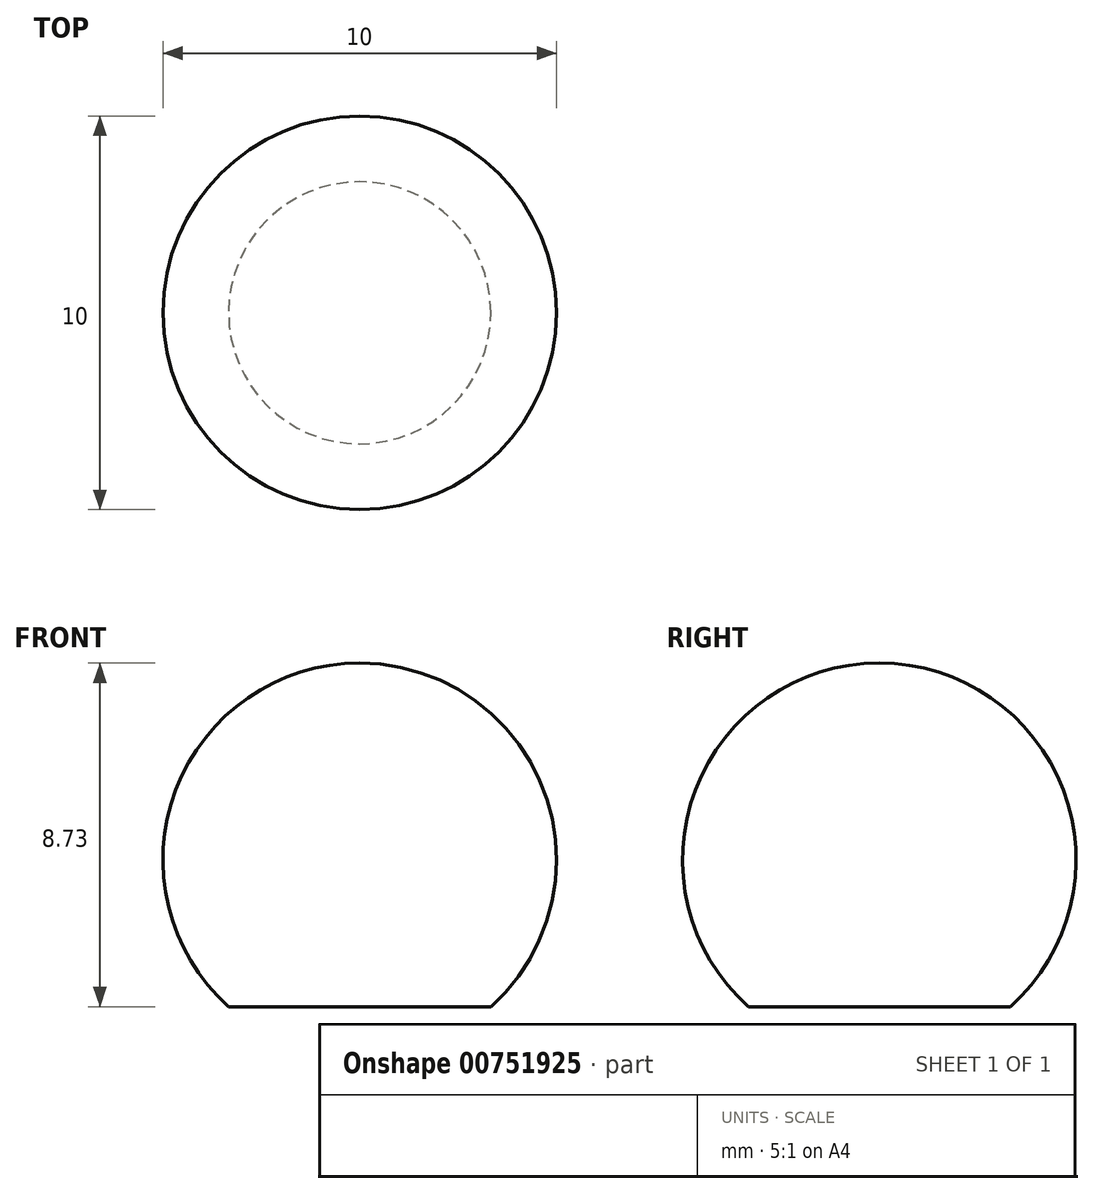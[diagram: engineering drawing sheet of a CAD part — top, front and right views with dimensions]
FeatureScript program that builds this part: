
annotation { "Feature Type Name" : "Feature", "Feature Type Description" : "" }
export const myFeature = defineFeature(function(context is Context, id is Id, definition is map)
    precondition{}
    {
        {
            var Q0;
            Q0=qCreatedBy(makeId("Front.planeOp"),FACE);
            var sketch = newSketch(context, id + "F0", { "sketchPlane" : qUnion([Q0])});
            skLineSegment(sketch, "E0", {"start": v(0, 5) * mm, "end": v(0, -5) * mm, "construction": true});
            skArc(sketch, "E1", {"start": v(0, -5) * mm, "mid": v(5, 0) * mm, "end": v(0, 5) * mm});
            skPoint(sketch, "E2", {"position": v(0, -3.73) * mm});
            skLineSegment(sketch, "E3", {"start": v(0, -3.73) * mm, "end": v(3.33, -3.73) * mm});
            skPoint(sketch, "E4", {"position": v(3.33, -3.73) * mm});
            skLineSegment(sketch, "E5", {"start": v(0, 5) * mm, "end": v(0, -3.73) * mm});
            skSolve(sketch);
        }
        {
            var Q0;
            Q0 = qSketchRegion(id + "F0", true);
            var Q1;
            Q1=sQuery(id+"F0.wireOp",EDGE,"E0");
            revolve(context, id + "F1", {"surfaceOperationType" : NewSurfaceOperationType.NEW, "entities" : qUnion([Q0]), "axis" : qUnion([Q1]), "revolveType" : RevolveType.FULL});
        }
    });
